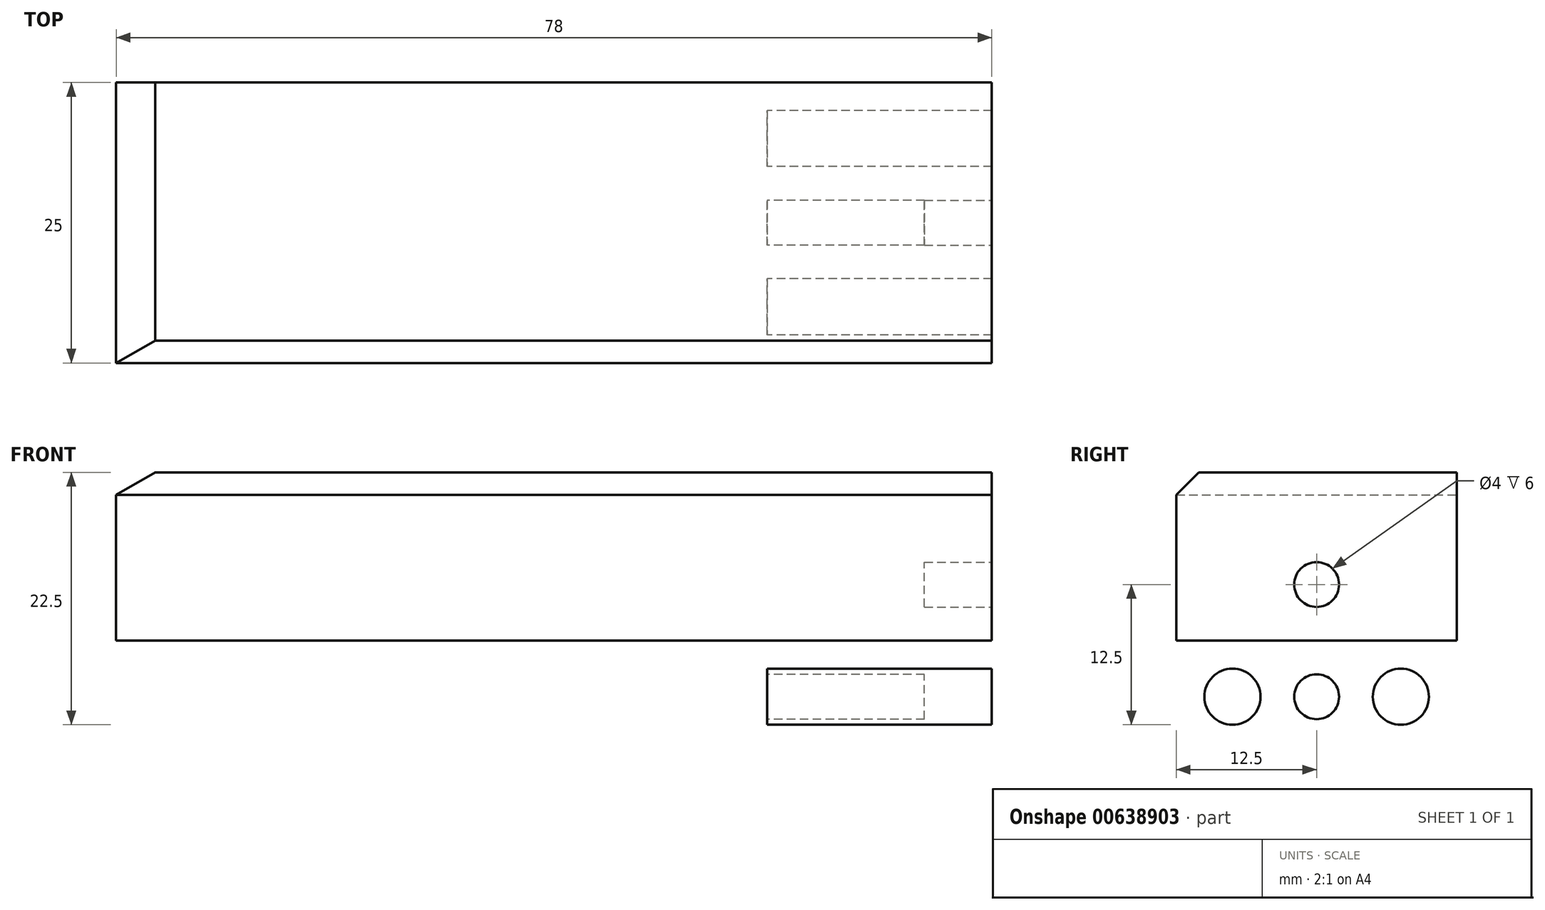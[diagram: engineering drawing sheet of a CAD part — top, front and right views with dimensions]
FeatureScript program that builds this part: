
annotation { "Feature Type Name" : "Feature", "Feature Type Description" : "" }
export const myFeature = defineFeature(function(context is Context, id is Id, definition is map)
    precondition{}
    {
        {
            var Q0;
            Q0=qCreatedBy(makeId("Front.planeOp"),FACE);
            var sketch = newSketch(context, id + "F0", { "sketchPlane" : qUnion([Q0])});
            skLineSegment(sketch, "E0", {"start": v(-54.49, 10.5) * mm, "end": v(-56.49, 12.5) * mm});
            skLineSegment(sketch, "E1", {"start": v(-79.49, -2.5) * mm, "end": v(-54.49, -2.5) * mm});
            skLineSegment(sketch, "E2", {"start": v(-79.49, 10.5) * mm, "end": v(-54.49, 10.5) * mm});
            skLineSegment(sketch, "E3", {"start": v(-56.49, 12.5) * mm, "end": v(-79.49, 12.5) * mm});
            skLineSegment(sketch, "E4", {"start": v(-59.49, -12) * mm, "end": v(-59.49, -3) * mm});
            skLineSegment(sketch, "E5", {"start": v(-63.99, -7.5) * mm, "end": v(-54.99, -7.5) * mm});
            skLineSegment(sketch, "E6", {"start": v(-74.49, -12) * mm, "end": v(-74.49, -3) * mm});
            skLineSegment(sketch, "E7", {"start": v(-78.99, -7.5) * mm, "end": v(-69.99, -7.5) * mm});
            skLineSegment(sketch, "E8", {"start": v(-66.99, -11.5) * mm, "end": v(-66.99, -3.5) * mm});
            skLineSegment(sketch, "E9", {"start": v(-70.99, -7.5) * mm, "end": v(-62.99, -7.5) * mm});
            skLineSegment(sketch, "E10", {"start": v(-66.99, -1.5) * mm, "end": v(-66.99, 6.5) * mm});
            skLineSegment(sketch, "E11", {"start": v(-70.99, 2.5) * mm, "end": v(-62.99, 2.5) * mm});
            skCircle(sketch, "E12", {"center": v(-66.99, 2.5) * mm, "radius": 2 * mm});
            skCircle(sketch, "E13", {"center": v(-66.99, -7.5) * mm, "radius": 2 * mm});
            skCircle(sketch, "E14", {"center": v(-59.49, -7.5) * mm, "radius": 2.5 * mm});
            skCircle(sketch, "E15", {"center": v(-74.49, -7.5) * mm, "radius": 2.5 * mm});
            skLineSegment(sketch, "E16", {"start": v(-54.49, 10.5) * mm, "end": v(-54.49, -12.5) * mm});
            skLineSegment(sketch, "E17", {"start": v(-79.49, -12.5) * mm, "end": v(-79.49, 12.5) * mm});
            skLineSegment(sketch, "E18", {"start": v(-79.49, -12.5) * mm, "end": v(-54.49, -12.5) * mm});
            skLineSegment(sketch, "E19", {"start": v(-0.51, 10.5) * mm, "end": v(77.49, 10.5) * mm});
            skLineSegment(sketch, "E20", {"start": v(55.49, -7.5) * mm, "end": v(79.49, -7.5) * mm});
            skLineSegment(sketch, "E21", {"start": v(69.62, 2.5) * mm, "end": v(78.2, 2.5) * mm});
            skLineSegment(sketch, "E22", {"start": v(71.49, 0.5) * mm, "end": v(70.33, 2.5) * mm});
            skLineSegment(sketch, "E23", {"start": v(71.49, 4.5) * mm, "end": v(70.33, 2.5) * mm});
            skLineSegment(sketch, "E24", {"start": v(71.49, 4.5) * mm, "end": v(77.49, 4.5) * mm});
            skLineSegment(sketch, "E25", {"start": v(71.49, 0.5) * mm, "end": v(71.49, 4.5) * mm});
            skLineSegment(sketch, "E26", {"start": v(77.49, 0.5) * mm, "end": v(71.49, 0.5) * mm});
            skLineSegment(sketch, "E27", {"start": v(57.49, -2.5) * mm, "end": v(57.49, -12.5) * mm});
            skLineSegment(sketch, "E28", {"start": v(57.49, -2.5) * mm, "end": v(-0.51, -2.5) * mm});
            skLineSegment(sketch, "E29", {"start": v(77.49, -12.5) * mm, "end": v(57.49, -12.5) * mm});
            skLineSegment(sketch, "E30", {"start": v(77.49, 12.5) * mm, "end": v(77.49, -12.5) * mm});
            skLineSegment(sketch, "E31", {"start": v(2.95, 12.5) * mm, "end": v(77.49, 12.5) * mm});
            skLineSegment(sketch, "E32", {"start": v(-0.51, 10.5) * mm, "end": v(-0.51, -2.5) * mm});
            skLineSegment(sketch, "E33", {"start": v(-0.51, 10.5) * mm, "end": v(2.95, 12.5) * mm});
            skSolve(sketch);
        }
        {
            var Q0;
            {var subQ5=sQuery(id+"F0.wireOp",EDGE,"E26");Q0=makeQuery(id+"F0.imprint","IMPRINT",FACE,{"disambiguationData":[TD([[makeQuery(id+"F0.imprint","IMPRINT",EDGE,{"derivedFrom":subQ5}),-1.0]])]});}
            var Q1;
            {var subQ0=sQuery(id+"F0.wireOp",EDGE,"E19");Q1=makeQuery(id+"F0.imprint","IMPRINT",FACE,{"disambiguationData":[TD([[makeQuery(id+"F0.imprint","IMPRINT",EDGE,{"derivedFrom":subQ0}),1.0]])]});}
            var Q2;
            {var subQ5=sQuery(id+"F0.wireOp",EDGE,"E29");Q2=makeQuery(id+"F0.imprint","IMPRINT",FACE,{"disambiguationData":[TD([[makeQuery(id+"F0.imprint","IMPRINT",EDGE,{"derivedFrom":subQ5}),-1.0]])]});}
            var Q3;
            {var subQ5=sQuery(id+"F0.wireOp",EDGE,"E24");Q3=makeQuery(id+"F0.imprint","IMPRINT",FACE,{"disambiguationData":[TD([[makeQuery(id+"F0.imprint","IMPRINT",EDGE,{"derivedFrom":subQ5}),-1.0]])]});}
            var Q4;
            {var subQ8=sQuery(id+"F0.wireOp",EDGE,"E19");Q4=makeQuery(id+"F0.imprint","IMPRINT",FACE,{"disambiguationData":[TD([[makeQuery(id+"F0.imprint","IMPRINT",EDGE,{"derivedFrom":subQ8}),-1.0]])]});}
            var Q5;
            {var subQ0=sQuery(id+"F0.wireOp",EDGE,"E22");Q5=makeQuery(id+"F0.imprint","IMPRINT",FACE,{"disambiguationData":[TD([[makeQuery(id+"F0.imprint","IMPRINT",EDGE,{"derivedFrom":subQ0}),-1.0]])]});}
            var Q6;
            {var subQ0=sQuery(id+"F0.wireOp",EDGE,"E23");Q6=makeQuery(id+"F0.imprint","IMPRINT",FACE,{"disambiguationData":[TD([[makeQuery(id+"F0.imprint","IMPRINT",EDGE,{"derivedFrom":subQ0}),1.0]])]});}
            extrude(context, id + "F1", {"entities" : qUnion([Q0, Q1, Q2, Q3, Q4, Q5, Q6]), "depth" : 25 * mm, "offsetDistance" : 25 * mm});
        }
        {
            var Q0;
            Q0=makeQuery(id+"F1.opExtrude","SWEPT_FACE",FACE,{"disambiguationData":[OSD([sQuery(id+"F0.wireOp",EDGE,"E27")])]});
            var sketch = newSketch(context, id + "F2", { "sketchPlane" : qUnion([Q0])});
            skLineSegment(sketch, "E34", {"start": v(25, 10.5) * mm, "end": v(23, 12.5) * mm});
            skLineSegment(sketch, "E35", {"start": v(0, -2.5) * mm, "end": v(25, -2.5) * mm});
            skLineSegment(sketch, "E36", {"start": v(0, 10.5) * mm, "end": v(25, 10.5) * mm});
            skLineSegment(sketch, "E37", {"start": v(23, 12.5) * mm, "end": v(0, 12.5) * mm});
            skCircle(sketch, "E38", {"center": v(12.5, 2.5) * mm, "radius": 2 * mm});
            skCircle(sketch, "E39", {"center": v(12.5, -7.5) * mm, "radius": 2 * mm});
            skCircle(sketch, "E40", {"center": v(20, -7.5) * mm, "radius": 2.5 * mm});
            skCircle(sketch, "E41", {"center": v(5, -7.5) * mm, "radius": 2.5 * mm});
            skLineSegment(sketch, "E42", {"start": v(25, 10.5) * mm, "end": v(25, -12.5) * mm});
            skLineSegment(sketch, "E43", {"start": v(0, -12.5) * mm, "end": v(0, 12.5) * mm});
            skLineSegment(sketch, "E44", {"start": v(0, -12.5) * mm, "end": v(25, -12.5) * mm});
            skLineSegment(sketch, "E45.0", {"start": v(0, -2.5) * mm, "end": v(0, -12.5) * mm});
            skLineSegment(sketch, "E46.0", {"start": v(25, -12.5) * mm, "end": v(0, -12.5) * mm});
            skLineSegment(sketch, "E47.0", {"start": v(25, -2.5) * mm, "end": v(25, -12.5) * mm});
            skSolve(sketch);
        }
        {
            var Q0;
            Q0=makeQuery(id+"F2.imprint","IMPRINT",FACE,{"disambiguationData":[TD([[makeQuery(id+"F2.imprint","IMPRINT",EDGE,{"derivedFrom":sQuery(id+"F2.wireOp",EDGE,"E40")}),-1.0]])]});
            var Q1;
            Q1=makeQuery(id+"F2.imprint","IMPRINT",FACE,{"disambiguationData":[TD([[makeQuery(id+"F2.imprint","IMPRINT",EDGE,{"derivedFrom":sQuery(id+"F2.wireOp",EDGE,"E41")}),-1.0]])]});
            extrude(context, id + "F3", {"entities" : qUnion([Q0, Q1]), "operationType" : NewBodyOperationType.REMOVE, "endBound" : BoundingType.THROUGH_ALL, "oppositeDirection" : true, "depth" : 25 * mm, "offsetDistance" : 25 * mm});
        }
        {
            var Q0;
            Q0=makeQuery(id+"F1.opExtrude","SWEPT_FACE",FACE,{"disambiguationData":[OSD([sQuery(id+"F0.wireOp",EDGE,"E30")])]});
            var sketch = newSketch(context, id + "F4", { "sketchPlane" : qUnion([Q0])});
            skCircle(sketch, "E48.0", {"center": v(-12.5, -7.5) * mm, "radius": 2 * mm});
            skCircle(sketch, "E49.0", {"center": v(-12.5, 2.5) * mm, "radius": 2 * mm});
            skSolve(sketch);
        }
        {
            var Q0;
            Q0=makeQuery(id+"F4.imprint","IMPRINT",FACE,{"disambiguationData":[TD([[makeQuery(id+"F4.imprint","IMPRINT",EDGE,{"derivedFrom":sQuery(id+"F4.wireOp",EDGE,"E49.0")}),1.0]])]});
            var Q1;
            Q1=makeQuery(id+"F4.imprint","IMPRINT",FACE,{"disambiguationData":[TD([[makeQuery(id+"F4.imprint","IMPRINT",EDGE,{"derivedFrom":sQuery(id+"F4.wireOp",EDGE,"E48.0")}),1.0]])]});
            extrude(context, id + "F5", {"entities" : qUnion([Q0, Q1]), "operationType" : NewBodyOperationType.REMOVE, "oppositeDirection" : true, "depth" : 6 * mm, "offsetDistance" : 25 * mm});
        }
        {
            var Q0;
            Q0=makeQuery(id+"F1.opExtrude","CAP_EDGE",EDGE,{"disambiguationData":[OSD([sQuery(id+"F0.wireOp",EDGE,"E31")])],"isStart":false});
            chamfer(context, id + "F6", {"entities" : qUnion([Q0]), "width" : 2 * mm, "tangentPropagation" : true});
        }
    });
